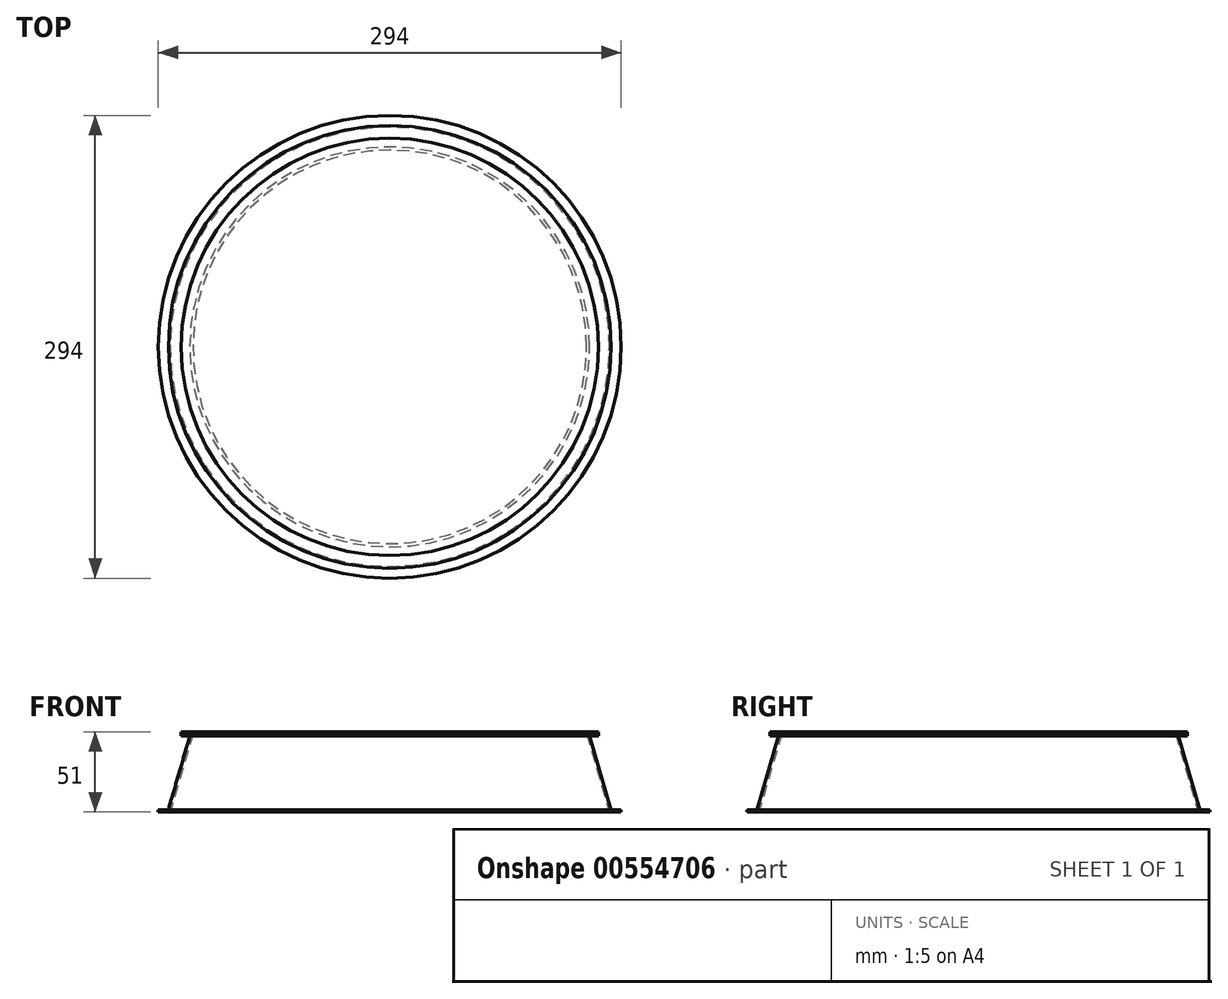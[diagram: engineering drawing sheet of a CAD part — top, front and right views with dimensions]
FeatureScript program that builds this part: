
annotation { "Feature Type Name" : "Feature", "Feature Type Description" : "" }
export const myFeature = defineFeature(function(context is Context, id is Id, definition is map)
    precondition{}
    {
        {
            var Q0;
            Q0=qCreatedBy(makeId("Front.planeOp"),FACE);
            var sketch = newSketch(context, id + "F0", { "sketchPlane" : qUnion([Q0])});
            skLineSegment(sketch, "E0.top", {"start": v(-147, -25) * mm, "end": v(-139.5, -25) * mm});
            skLineSegment(sketch, "E0.left", {"start": v(-147, -23.5) * mm, "end": v(-147, -25) * mm});
            skLineSegment(sketch, "E0.right", {"start": v(147, 25) * mm, "end": v(147, -25) * mm});
            skPoint(sketch, "E0.middle", {"position": v(0, 0) * mm});
            skLineSegment(sketch, "E1", {"start": v(-147, -23.5) * mm, "end": v(-147, -23.5) * mm});
            skLineSegment(sketch, "E2.left", {"start": v(132.5, 25) * mm, "end": v(132.5, 23.5) * mm});
            skLineSegment(sketch, "E2.right", {"start": v(-132.5, 25) * mm, "end": v(-132.5, 23.5) * mm});
            skPoint(sketch, "E2.middle", {"position": v(0, 25) * mm});
            skPoint(sketch, "E3.orphan", {"position": v(132.5, 26.5) * mm});
            skPoint(sketch, "E4.orphan", {"position": v(-132.5, 26.5) * mm});
            skPoint(sketch, "E5", {"position": v(-139.5, -25) * mm});
            skPoint(sketch, "E6", {"position": v(-125, 25) * mm});
            skLineSegment(sketch, "E7", {"start": v(-125, 25) * mm, "end": v(-139.07, -23.5) * mm});
            skLineSegment(sketch, "E8", {"start": v(-127.1, 23.13) * mm, "end": v(-139.53, -19.73) * mm});
            skLineSegment(sketch, "E9", {"start": v(-139.53, -19.73) * mm, "end": v(-140.63, -23.5) * mm});
            skLineSegment(sketch, "E10", {"start": v(-127.1, 23.13) * mm, "end": v(-127, 23.5) * mm});
            skPoint(sketch, "E11.trimOffspring.end.orphan", {"position": v(147, -23.5) * mm});
            skLineSegment(sketch, "E12", {"start": v(-132.5, 25) * mm, "end": v(-125, 25) * mm});
            skLineSegment(sketch, "E13", {"start": v(-126.94, 23.5) * mm, "end": v(-132.5, 23.5) * mm});
            skLineSegment(sketch, "E14", {"start": v(-147, -23.5) * mm, "end": v(-140.63, -23.5) * mm});
            skLineSegment(sketch, "E15", {"start": v(-140.63, -23.5) * mm, "end": v(-140.63, -23.5) * mm});
            skLineSegment(sketch, "E16", {"start": v(-139.07, -23.5) * mm, "end": v(-139.5, -25) * mm});
            skPoint(sketch, "E0.bottom.start.orphan", {"position": v(-147, 25) * mm});
            skLineSegment(sketch, "E17.trimOffspring", {"start": v(0, 25) * mm, "end": v(147, 25) * mm});
            skLineSegment(sketch, "E18", {"start": v(0, 0) * mm, "end": v(0, 25) * mm});
            skSolve(sketch);
        }
        {
            var Q0;
            Q0=makeQuery(id+"F0.imprint","IMPRINT",FACE,{"disambiguationData":[TD([[makeQuery(id+"F0.imprint","IMPRINT",EDGE,{"derivedFrom":sQuery(id+"F0.wireOp",EDGE,"E0.top")}),1.0]])]});
            var Q1;
            Q1=sQuery(id+"F0.wireOp",EDGE,"E18");
            revolve(context, id + "F1", {"entities" : qUnion([Q0]), "axis" : qUnion([Q1]), "revolveType" : RevolveType.FULL});
        }
        {
            var Q0;
            Q0=makeQuery(id+"F1.opRevolve","SWEPT_FACE",FACE,{"disambiguationData":[OSD([sQuery(id+"F0.wireOp",EDGE,"E12")])]});
            var sketch = newSketch(context, id + "F2", { "sketchPlane" : qUnion([Q0])});
            skCircle(sketch, "E19.0", {"center": v(0, 0) * mm, "radius": 132.5 * mm});
            skSolve(sketch);
        }
        {
            var Q0;
            Q0 = qSketchRegion(id + "F2", true);
            var Q1;
            Q1=makeQuery(id+"F2.imprint","IMPRINT",FACE,{"disambiguationData":[TD([[makeQuery(id+"F2.imprint","IMPRINT",EDGE,{"derivedFrom":makeQuery(id+"F1.opRevolve","SWEPT_EDGE",EDGE,{"disambiguationData":[OSD([sQuery(id+"F0.wireOp",EDGE,"E7"),sQuery(id+"F0.wireOp",EDGE,"E12")])]})}),-1.0]])]});
            extrude(context, id + "F3", {"entities" : qUnion([Q0, Q1]), "depth" : 1 * mm, "offsetDistance" : 25 * mm});
        }
    });
